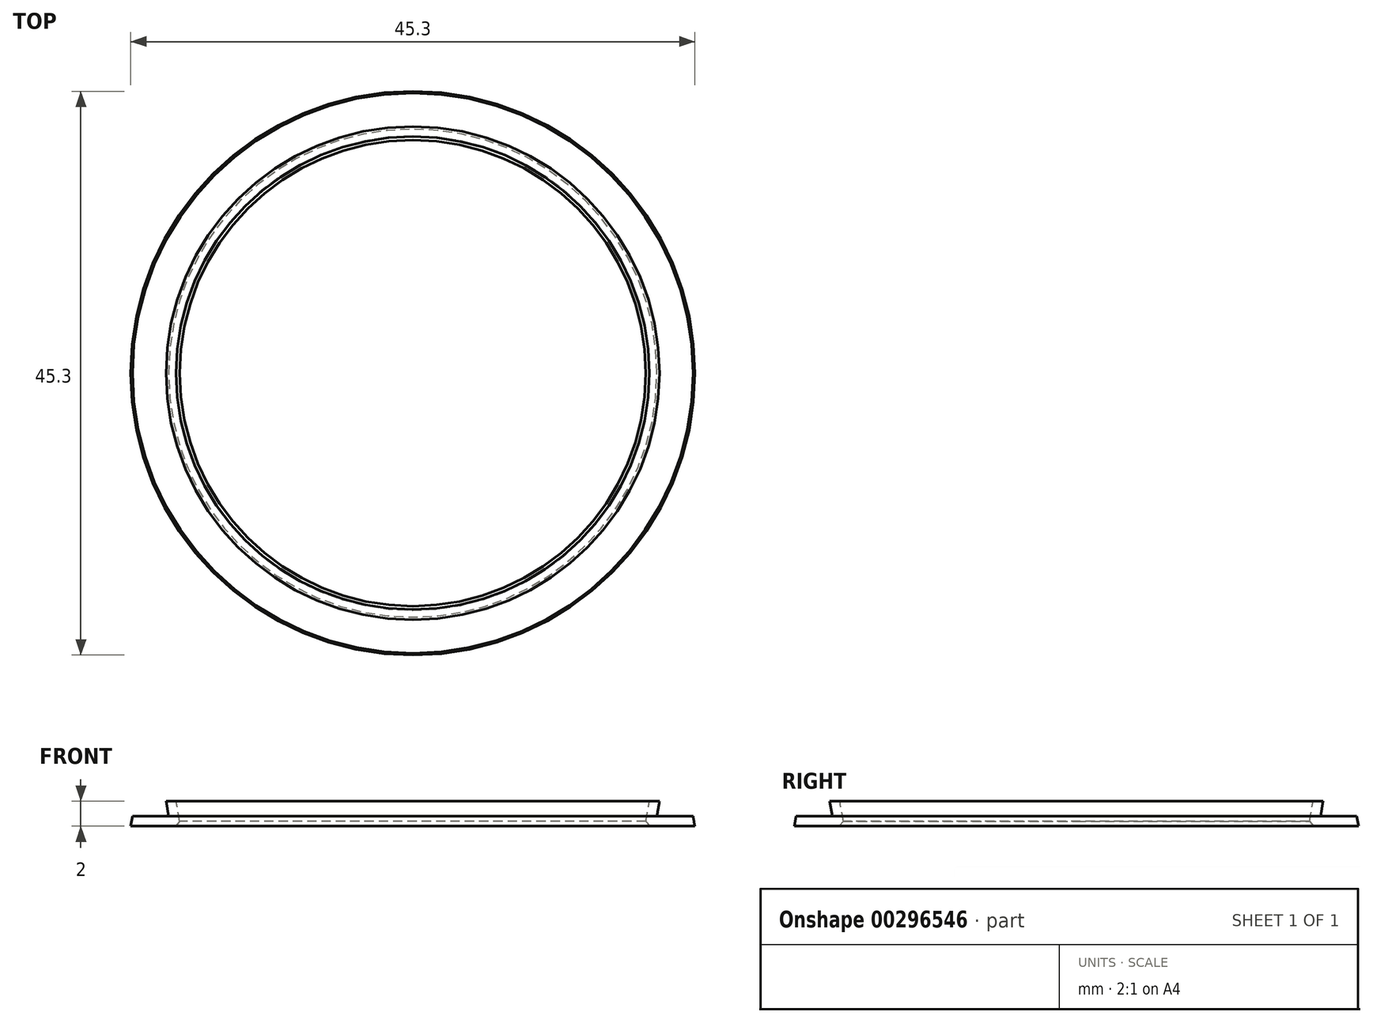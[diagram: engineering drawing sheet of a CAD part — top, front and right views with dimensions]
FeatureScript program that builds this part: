
annotation { "Feature Type Name" : "Feature", "Feature Type Description" : "" }
export const myFeature = defineFeature(function(context is Context, id is Id, definition is map)
    precondition{}
    {
        {
            var Q0;
            Q0=qCreatedBy(makeId("Top.planeOp"),FACE);
            var sketch = newSketch(context, id + "F0", { "sketchPlane" : qUnion([Q0])});
            skCircle(sketch, "E0", {"center": v(0, 0) * mm, "radius": 18.65 * mm});
            skCircle(sketch, "E1.0", {"center": v(0, 0) * mm, "radius": 22.65 * mm});
            skSolve(sketch);
        }
        {
            var Q0;
            Q0=makeQuery(id+"F0.imprint","IMPRINT",FACE,{"disambiguationData":[TD([[makeQuery(id+"F0.imprint","IMPRINT",EDGE,{"derivedFrom":sQuery(id+"F0.wireOp",EDGE,"E0")}),-1.0]])]});
            extrude(context, id + "F1", {"entities" : qUnion([Q0]), "depth" : 2 * mm, "hasDraft" : true, "draftAngle" : 10 * degree, "draftPullDirection" : true});
        }
        {
            var Q0;
            Q0=makeQuery(id+"F1.opExtrude","CAP_FACE",FACE,{"disambiguationData":[OSD([sQuery(id+"F0.wireOp",EDGE,"E0"),sQuery(id+"F0.wireOp",EDGE,"E1.0")])],"isStart":false});
            var Q1;
            Q1=makeQuery(id+"F1.opExtrude","SWEPT_FACE",FACE,{"disambiguationData":[OSD([sQuery(id+"F0.wireOp",EDGE,"E1.0")])]});
            shell(context, id + "F2", {"entities" : qUnion([Q0, Q1]), "thickness" : 0.8 * mm});
        }
        {
            var Q0;
            Q0=makeQuery(id+"F1.opExtrude","CAP_EDGE",EDGE,{"disambiguationData":[OSD([sQuery(id+"F0.wireOp",EDGE,"E0")])],"isStart":true});
            chamfer(context, id + "F3", {"entities" : qUnion([Q0]), "width" : 0.4 * mm, "tangentPropagation" : true});
        }
    });
